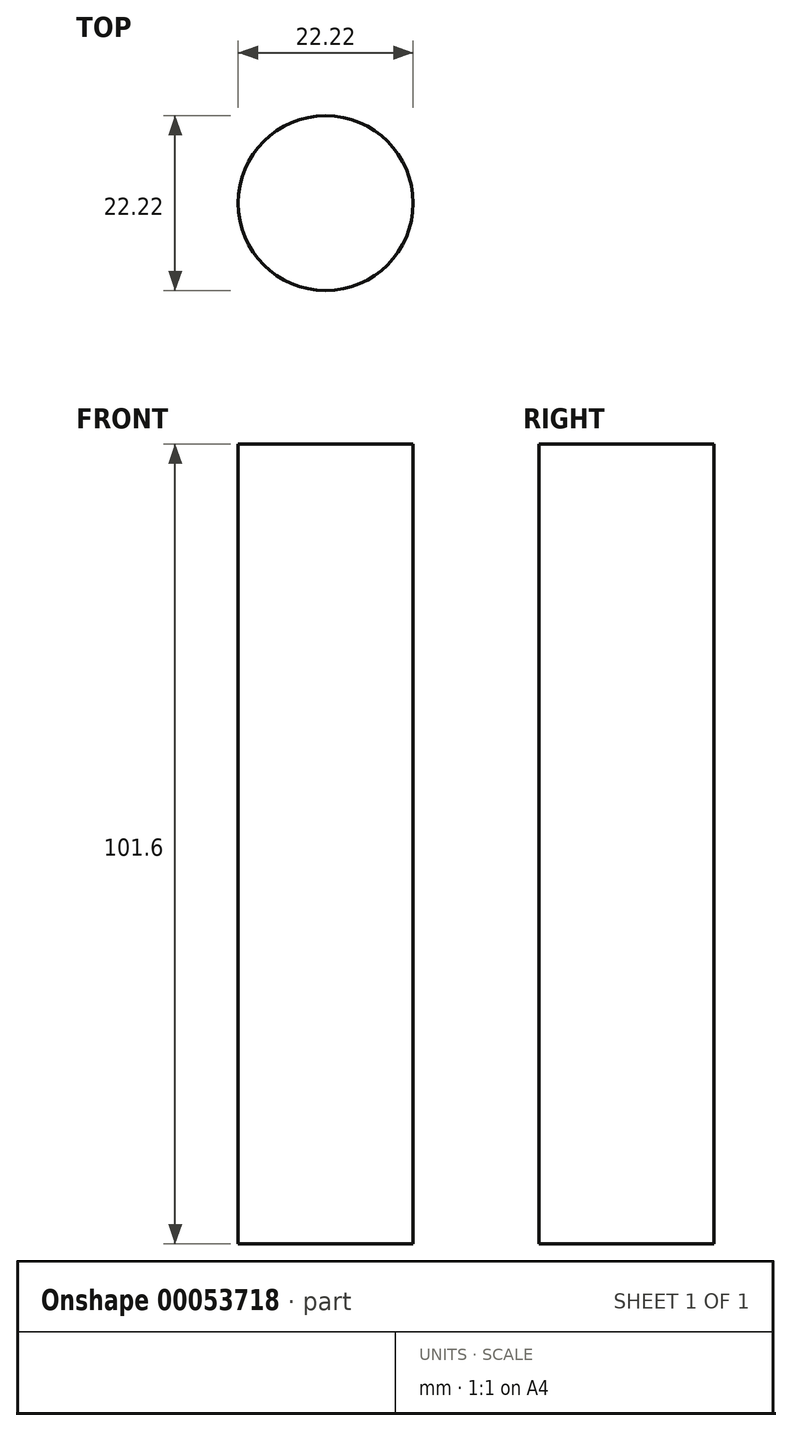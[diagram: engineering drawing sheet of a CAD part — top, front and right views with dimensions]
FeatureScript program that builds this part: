
annotation { "Feature Type Name" : "Feature", "Feature Type Description" : "" }
export const myFeature = defineFeature(function(context is Context, id is Id, definition is map)
    precondition{}
    {
        {
            var Q0;
            Q0=qCreatedBy(makeId("Top.planeOp"),FACE);
            var sketch = newSketch(context, id + "F0", { "sketchPlane" : qUnion([Q0])});
            skCircle(sketch, "E0", {"center": v(0, 0) * mm, "radius": 11.11 * mm});
            skSolve(sketch);
        }
        {
            var Q0;
            Q0 = qSketchRegion(id + "F0", true);
            extrude(context, id + "F1", {"entities" : qUnion([Q0]), "depth" : 101.6 * mm});
        }
    });
